# Revit family: F2AI_2903-2943-2606_OS275
name_source: partatom
category: Finestre
units: mm (PartAtom-declared; Revit-internal decimal feet)

## family parameters
Condiviso = No
Host = Muro
Numero OmniClass = 23.30.20.00
Punto di calcolo locali = Sì
Sempre verticale = Sì
Taglio con vuoti quando caricato = No
Titolo OmniClass = Windows

## types (4) — shared parameters
Altezza = 1500 mm  [stored 4.92126 ft]
Altezza di default del davanzale = 800 mm
Chiusura muro = Per host
Costruzione analitica = <Nessuno>
Descrizione = Finestra 2 ante battente apertura interna
H = 1500 mm  [stored 4.92126 ft]
H1 = 1500 mm  [stored 4.92126 ft]
H_Max = 2900 mm
H_Min = 300 mm
H_man = 500 mm  [stored 1.64042 ft]
H_maniglia = 500 mm  [stored 1.64042 ft]
H_vetro = 1424 mm  [stored 4.67192 ft]
L_Max = 2000 mm  [stored 6.56168 ft]
L_Min = 600 mm
Maniglia_alta = 1050 mm  [stored 3.44488 ft]
Maniglia_bassa = 750 mm  [stored 2.46063 ft]
Maniglia_media = 500 mm  [stored 1.64042 ft]
Modello = OS2 75
Produttore = Secco Sistemi Spa
URL = https://www.seccosistemi.com
WARNING = No
n2_cerniere = 2
n2_scarichi = 2
n3_cerniere = 3
n3_scarichi = 3
n4_cerniere = 4
numero_cerniere = 3

## per-type parameters (varying)
| type | L | L1 | L_vetro | Larghezza | Larghezza_1A | Larghezza_2A | MATERIALE | numero_scarichi |
| Acciao Corten | 1000 mm  [stored 3.28084 ft] | 1000 mm  [stored 3.28084 ft] | 440 mm | 1000 mm  [stored 3.28084 ft] | 516 mm  [stored 1.69291 ft] | 516 mm  [stored 1.69291 ft] | Acciaio corten | 2 |
| Acciaio inox | 1000 mm  [stored 3.28084 ft] | 1000 mm  [stored 3.28084 ft] | 440 mm | 1000 mm  [stored 3.28084 ft] | 516 mm  [stored 1.69291 ft] | 516 mm  [stored 1.69291 ft] | Acciaio inox, spazzolato | 2 |
| Acciaio zincato | 1000 mm  [stored 3.28084 ft] | 1000 mm  [stored 3.28084 ft] | 440 mm | 1000 mm  [stored 3.28084 ft] | 516 mm  [stored 1.69291 ft] | 516 mm  [stored 1.69291 ft] | Acciaio | 2 |
| Ottone | 2000 mm  [stored 6.56168 ft] | 2000 mm  [stored 6.56168 ft] | 940 mm  [stored 3.08399 ft] | 2000 mm  [stored 6.56168 ft] | 1016 mm | 1016 mm | Ottone | 3 |

note: [stored X ft] marks values corroborated as IEEE doubles in the binary element streams (Revit-internal decimal feet)
